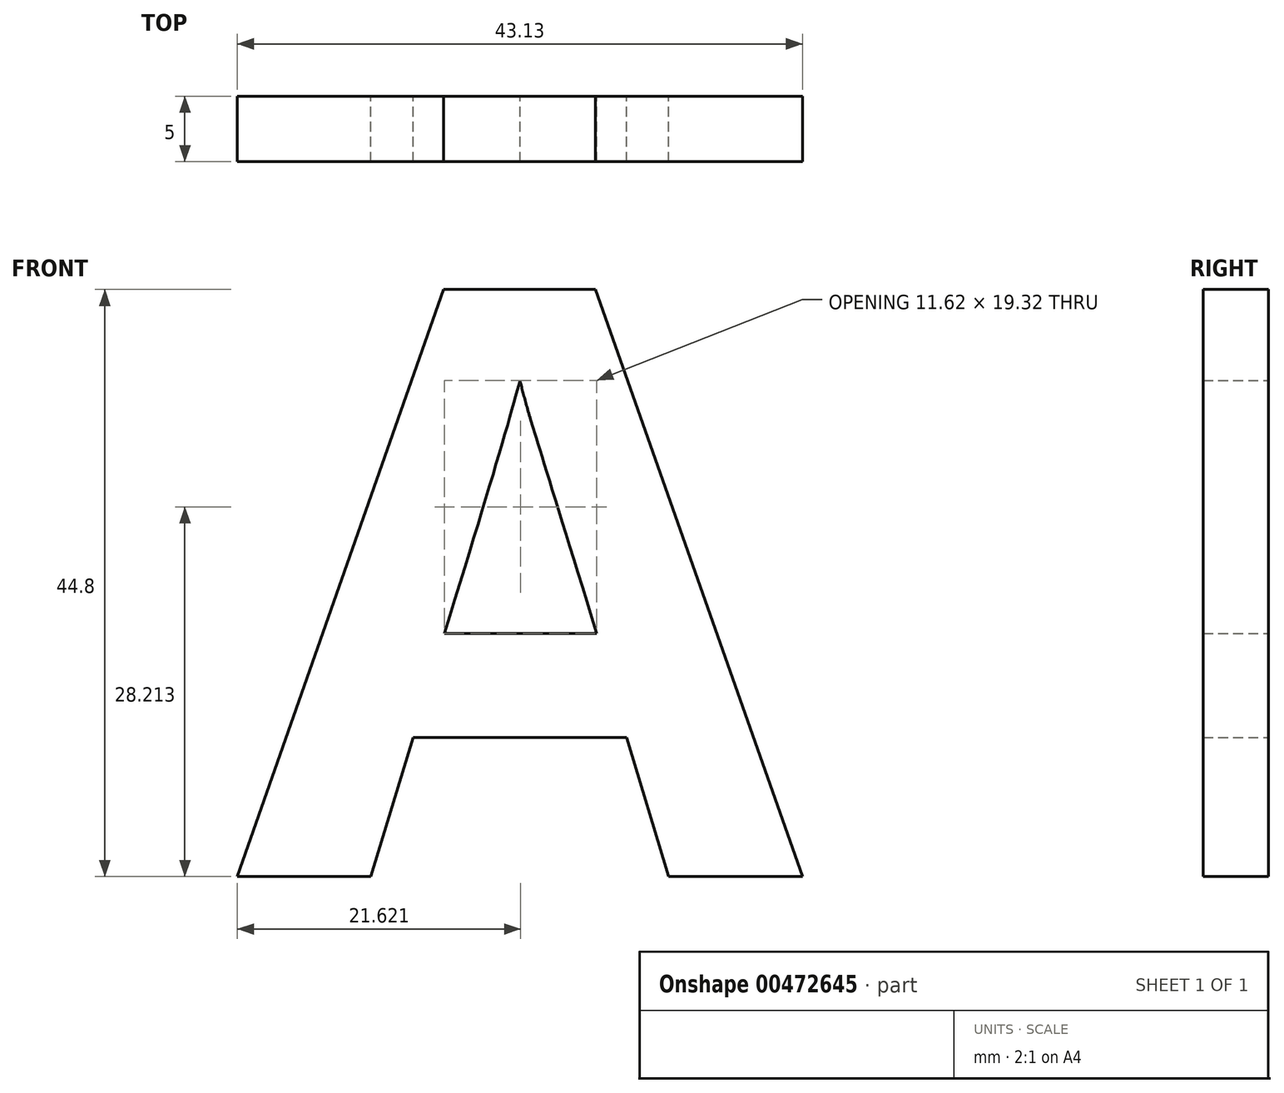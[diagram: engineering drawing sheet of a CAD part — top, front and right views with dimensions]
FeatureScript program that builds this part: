
annotation { "Feature Type Name" : "Feature", "Feature Type Description" : "" }
export const myFeature = defineFeature(function(context is Context, id is Id, definition is map)
    precondition{}
    {
        {
            var Q0;
            Q0=qCreatedBy(makeId("Front.planeOp"),FACE);
            var sketch = newSketch(context, id + "F0", { "sketchPlane" : qUnion([Q0])});
            skText(sketch, "E0", { "text": "A", "fontName": "OpenSans-Bold.ttf"});
            const initialGuessF0  = {"E0": [-0.00659, 0, 1, 0, 0.045]};
            skSetInitialGuess(sketch, initialGuessF0);
            skSolve(sketch);
        }
        {
            var Q0;
            Q0=makeQuery(id+"F0.imprint","IMPRINT",FACE,{"disambiguationData":[TD([[makeQuery(id+"F0.imprint","IMPRINT",EDGE,{"derivedFrom":sQuery(id+"F0.wireOp",EDGE,"E0.sketch_text.stroke-0")}),-1.0]])]});
            extrude(context, id + "F1", {"entities" : qUnion([Q0]), "depth" : 5 * mm});
        }
    });
